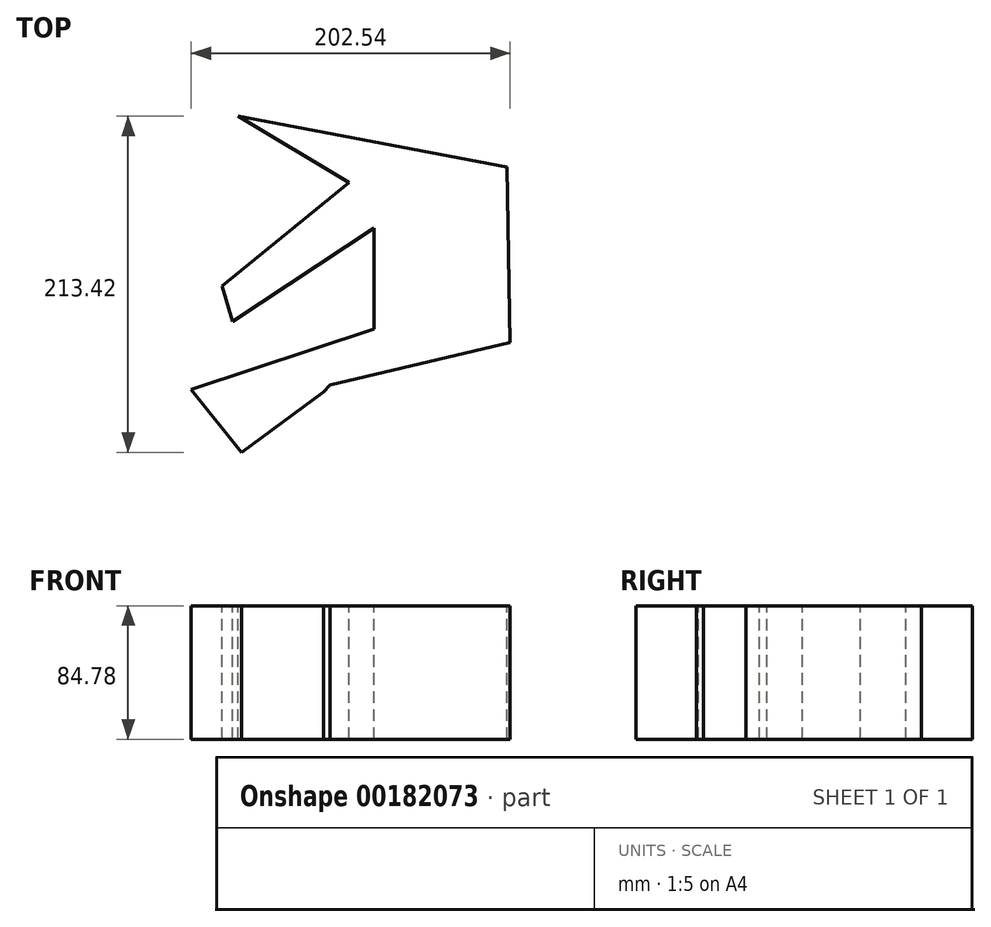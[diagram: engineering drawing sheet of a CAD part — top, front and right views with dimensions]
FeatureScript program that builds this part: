
annotation { "Feature Type Name" : "Feature", "Feature Type Description" : "" }
export const myFeature = defineFeature(function(context is Context, id is Id, definition is map)
    precondition{}
    {
        {
            var Q0;
            Q0=qCreatedBy(makeId("Top.planeOp"),FACE);
            var sketch = newSketch(context, id + "F0", { "sketchPlane" : qUnion([Q0])});
            skLineSegment(sketch, "E0", {"start": v(11.5, -62.7) * mm, "end": v(126.04, -35.74) * mm});
            skLineSegment(sketch, "E1", {"start": v(126.04, -35.74) * mm, "end": v(124.16, 75.67) * mm});
            skLineSegment(sketch, "E2", {"start": v(124.16, 75.67) * mm, "end": v(-46.82, 107.86) * mm});
            skLineSegment(sketch, "E3", {"start": v(-46.82, 107.86) * mm, "end": v(23.62, 65.84) * mm});
            skLineSegment(sketch, "E4", {"start": v(23.62, 65.84) * mm, "end": v(-57.06, 0) * mm});
            skLineSegment(sketch, "E5", {"start": v(-57.06, 0) * mm, "end": v(-50.17, -22.57) * mm});
            skLineSegment(sketch, "E6", {"start": v(-50.17, -22.57) * mm, "end": v(39.71, 37) * mm});
            skLineSegment(sketch, "E7", {"start": v(39.71, 37) * mm, "end": v(39.71, -27.38) * mm});
            skLineSegment(sketch, "E8", {"start": v(39.71, -27.38) * mm, "end": v(-76.5, -65.84) * mm});
            skLineSegment(sketch, "E9", {"start": v(-76.5, -65.84) * mm, "end": v(-44.73, -105.56) * mm});
            skLineSegment(sketch, "E10", {"start": v(-44.73, -105.56) * mm, "end": v(7.52, -67.3) * mm});
            skLineSegment(sketch, "E11", {"start": v(7.52, -67.3) * mm, "end": v(11.5, -62.7) * mm});
            skSolve(sketch);
        }
        {
            var Q0;
            Q0=makeQuery(id+"F0.imprint","IMPRINT",FACE,{"disambiguationData":[TD([[makeQuery(id+"F0.imprint","IMPRINT",EDGE,{"derivedFrom":sQuery(id+"F0.wireOp",EDGE,"E0")}),1.0]])]});
            extrude(context, id + "F1", {"entities" : qUnion([Q0]), "oppositeDirection" : true, "depth" : 84.78 * mm});
        }
    });
